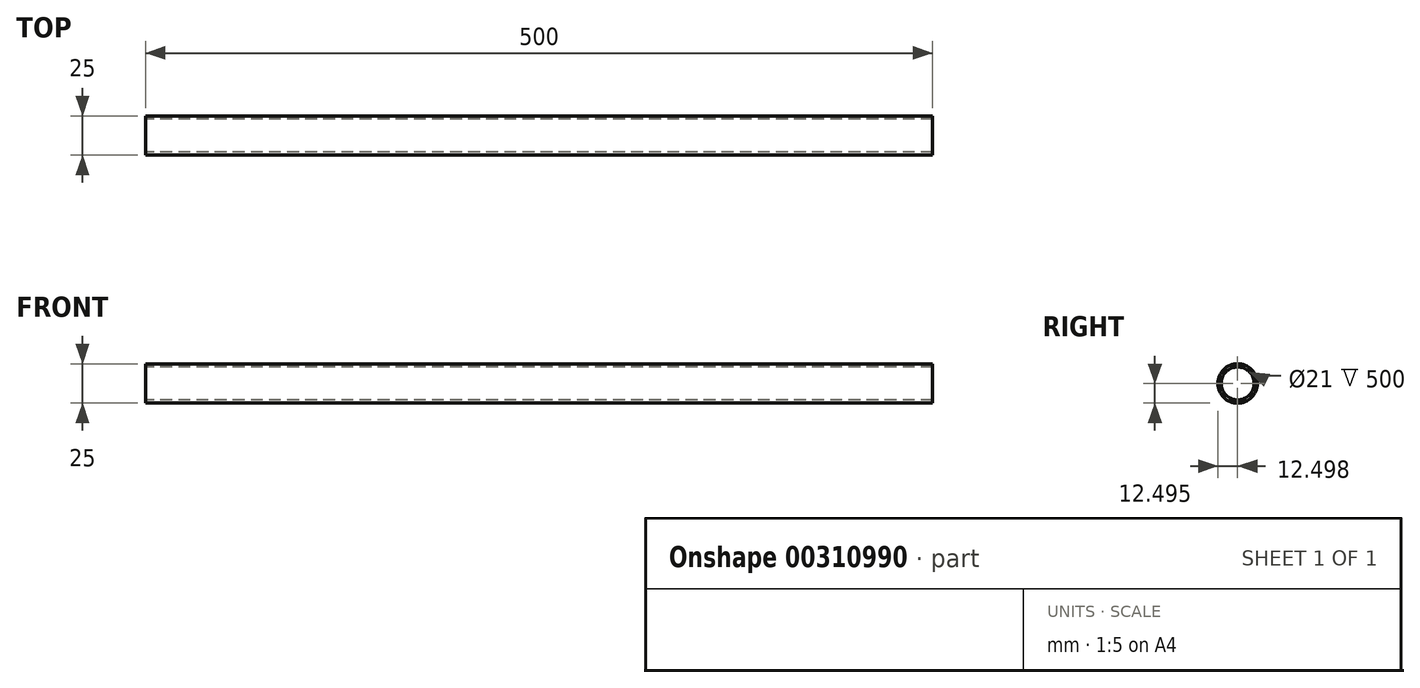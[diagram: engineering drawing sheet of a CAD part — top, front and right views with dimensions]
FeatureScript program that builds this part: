
annotation { "Feature Type Name" : "Feature", "Feature Type Description" : "" }
export const myFeature = defineFeature(function(context is Context, id is Id, definition is map)
    precondition{}
    {
        {
            var Q0;
            Q0=qCreatedBy(makeId("Right.planeOp"),FACE);
            var sketch = newSketch(context, id + "F0", { "sketchPlane" : qUnion([Q0])});
            skCircle(sketch, "E0", {"center": v(-27.82, 18.27) * mm, "radius": 12.5 * mm});
            skCircle(sketch, "E1", {"center": v(-27.82, 18.27) * mm, "radius": 10.5 * mm});
            skSolve(sketch);
        }
        {
            var Q0;
            Q0=makeQuery(id+"F0.imprint","IMPRINT",FACE,{"disambiguationData":[TD([[makeQuery(id+"F0.imprint","IMPRINT",EDGE,{"derivedFrom":sQuery(id+"F0.wireOp",EDGE,"E0")}),1.0]])]});
            extrude(context, id + "F1", {"entities" : qUnion([Q0]), "depth" : 500 * mm});
        }
    });
